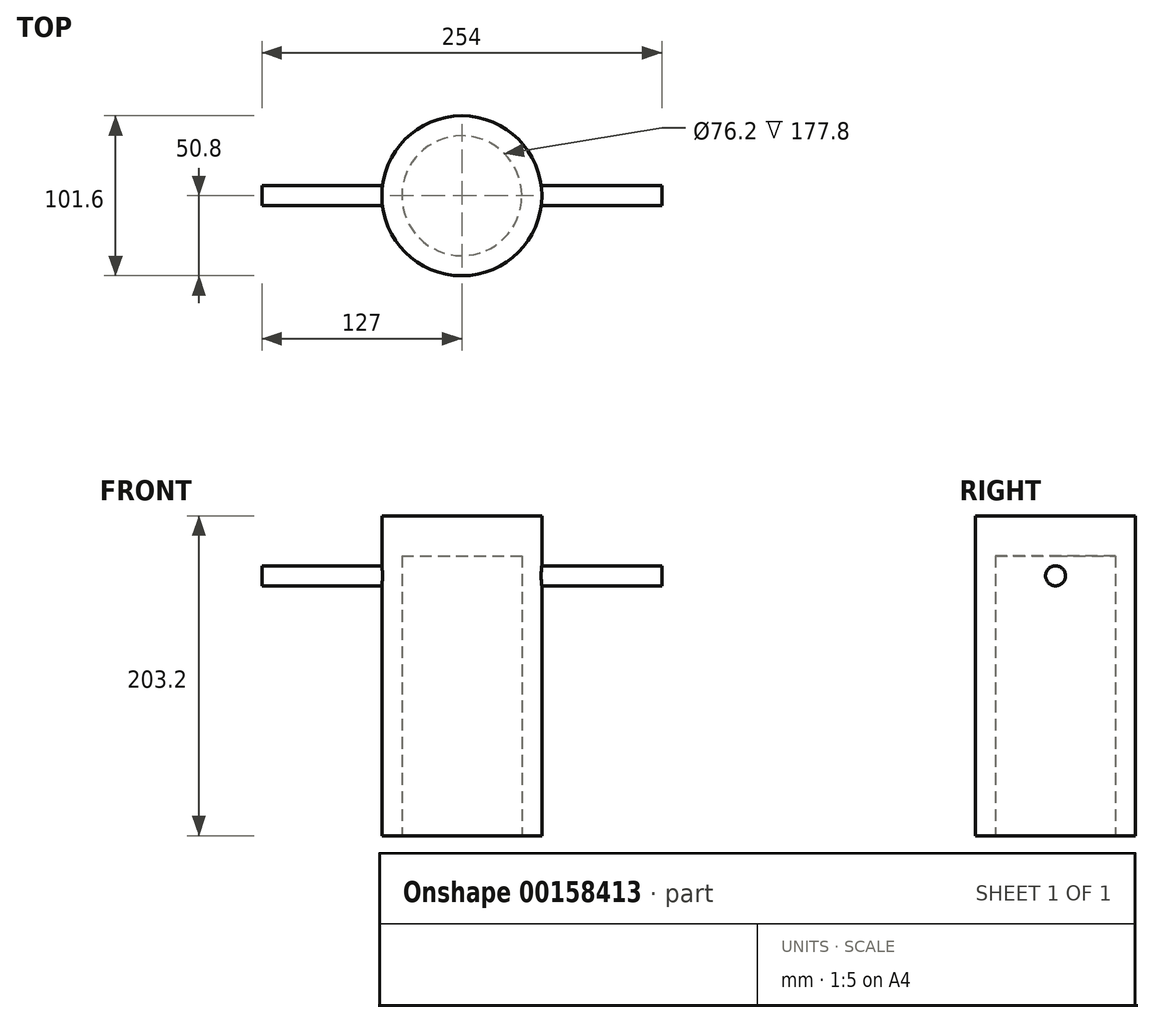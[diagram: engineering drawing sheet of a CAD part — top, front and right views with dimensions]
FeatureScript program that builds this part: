
annotation { "Feature Type Name" : "Feature", "Feature Type Description" : "" }
export const myFeature = defineFeature(function(context is Context, id is Id, definition is map)
    precondition{}
    {
        {
            var Q0;
            Q0=qCreatedBy(makeId("Top.planeOp"),FACE);
            var sketch = newSketch(context, id + "F0", { "sketchPlane" : qUnion([Q0])});
            skCircle(sketch, "E0", {"center": v(0, 0) * mm, "radius": 50.8 * mm});
            skSolve(sketch);
        }
        {
            var Q0;
            Q0=makeQuery(id+"F0.imprint","IMPRINT",FACE,{"disambiguationData":[TD([[makeQuery(id+"F0.imprint","IMPRINT",EDGE,{"derivedFrom":sQuery(id+"F0.wireOp",EDGE,"E0")}),1.0]])]});
            extrude(context, id + "F1", {"entities" : qUnion([Q0]), "depth" : 203.2 * mm});
        }
        {
            var Q0;
            Q0=qCreatedBy(makeId("Right.planeOp"),FACE);
            var sketch = newSketch(context, id + "F2", { "sketchPlane" : qUnion([Q0])});
            skCircle(sketch, "E1", {"center": v(0, 165.1) * mm, "radius": 6.35 * mm});
            skSolve(sketch);
        }
        {
            var Q0;
            Q0 = qSketchRegion(id + "F2", true);
            extrude(context, id + "F3", {"entities" : qUnion([Q0]), "operationType" : NewBodyOperationType.ADD, "depth" : 127 * mm, "hasSecondDirection" : true, "secondDirectionOppositeDirection" : true, "secondDirectionDepth" : 127 * mm});
        }
        {
            var Q0;
            Q0=makeQuery(id+"F1.opExtrude","CAP_FACE",FACE,{"disambiguationData":[OSD([sQuery(id+"F0.wireOp",EDGE,"E0")])],"isStart":true});
            var sketch = newSketch(context, id + "F4", { "sketchPlane" : qUnion([Q0])});
            skCircle(sketch, "E2.0", {"center": v(0, 0) * mm, "radius": 38.1 * mm});
            skSolve(sketch);
        }
        {
            var Q0;
            Q0=makeQuery(id+"F4.imprint","IMPRINT",FACE,{"disambiguationData":[TD([[makeQuery(id+"F4.imprint","IMPRINT",EDGE,{"derivedFrom":sQuery(id+"F4.wireOp",EDGE,"E2.0")}),1.0]])]});
            extrude(context, id + "F5", {"entities" : qUnion([Q0]), "operationType" : NewBodyOperationType.REMOVE, "oppositeDirection" : true, "depth" : 177.8 * mm});
        }
    });
